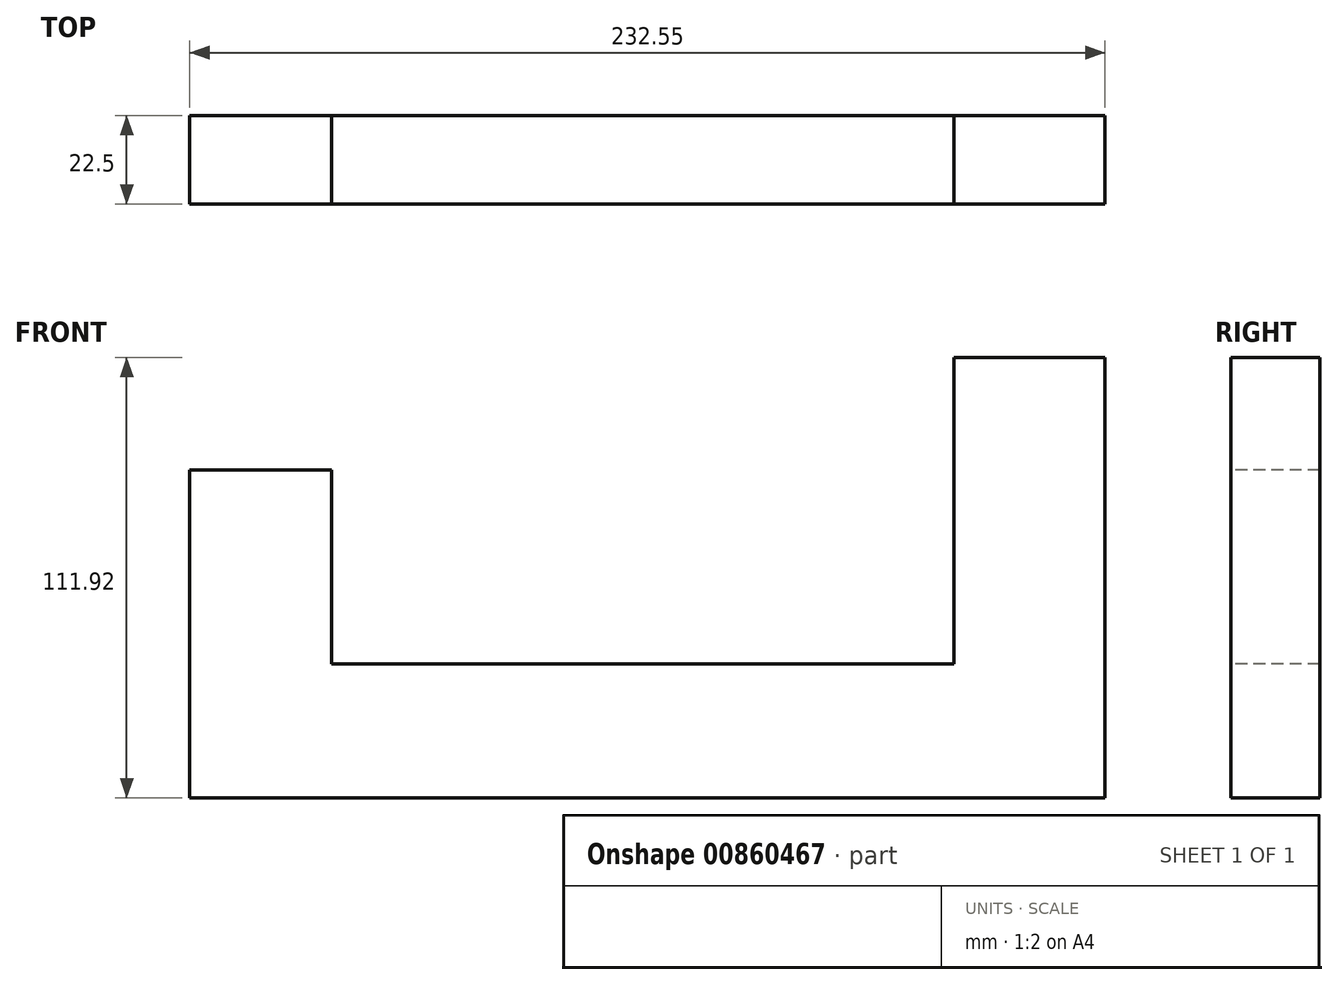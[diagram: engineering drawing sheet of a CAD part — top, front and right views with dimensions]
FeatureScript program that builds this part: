
annotation { "Feature Type Name" : "Feature", "Feature Type Description" : "" }
export const myFeature = defineFeature(function(context is Context, id is Id, definition is map)
    precondition{}
    {
        {
            var Q0;
            Q0=qCreatedBy(makeId("Front.planeOp"),FACE);
            var sketch = newSketch(context, id + "F0", { "sketchPlane" : qUnion([Q0])});
            skLineSegment(sketch, "E0.bottom", {"start": v(0, 0) * mm, "end": v(38.41, 0) * mm});
            skLineSegment(sketch, "E0.top", {"start": v(0, 111.92) * mm, "end": v(38.41, 111.92) * mm});
            skLineSegment(sketch, "E0.left", {"start": v(0, 0) * mm, "end": v(0, 111.92) * mm});
            skLineSegment(sketch, "E0.right", {"start": v(38.41, 0) * mm, "end": v(38.41, 111.92) * mm});
            skLineSegment(sketch, "E1.bottom", {"start": v(0, 0) * mm, "end": v(-158.1, 0) * mm});
            skLineSegment(sketch, "E1.top", {"start": v(0, 34.12) * mm, "end": v(-158.1, 34.12) * mm});
            skLineSegment(sketch, "E1.left", {"start": v(0, 0) * mm, "end": v(0, 34.12) * mm});
            skLineSegment(sketch, "E1.right", {"start": v(-158.1, 0) * mm, "end": v(-158.1, 34.12) * mm});
            skLineSegment(sketch, "E2.bottom", {"start": v(-158.1, 0) * mm, "end": v(-194.14, 0) * mm});
            skLineSegment(sketch, "E2.top", {"start": v(-158.1, 83.36) * mm, "end": v(-194.14, 83.36) * mm});
            skLineSegment(sketch, "E2.left", {"start": v(-158.1, 0) * mm, "end": v(-158.1, 83.36) * mm});
            skLineSegment(sketch, "E2.right", {"start": v(-194.14, 0) * mm, "end": v(-194.14, 83.36) * mm});
            skSolve(sketch);
        }
        {
            var Q0;
            Q0=makeQuery(id+"F0.imprint","IMPRINT",FACE,{"disambiguationData":[TD([[makeQuery(id+"F0.imprint","IMPRINT",EDGE,{"derivedFrom":sQuery(id+"F0.wireOp",EDGE,"E0.bottom")}),1.0]])]});
            var Q1;
            {var subQ0=sQuery(id+"F0.wireOp",EDGE,"E1.bottom");Q1=makeQuery(id+"F0.imprint","IMPRINT",FACE,{"disambiguationData":[TD([[makeQuery(id+"F0.imprint","IMPRINT",EDGE,{"derivedFrom":subQ0}),-1.0]])]});}
            var Q2;
            {var subQ3=sQuery(id+"F0.wireOp",EDGE,"E2.bottom");Q2=makeQuery(id+"F0.imprint","IMPRINT",FACE,{"disambiguationData":[TD([[makeQuery(id+"F0.imprint","IMPRINT",EDGE,{"derivedFrom":subQ3}),-1.0]])]});}
            extrude(context, id + "F1", {"entities" : qUnion([Q0, Q1, Q2]), "oppositeDirection" : true, "depth" : 22.5 * mm, "offsetDistance" : 25 * mm});
        }
    });
